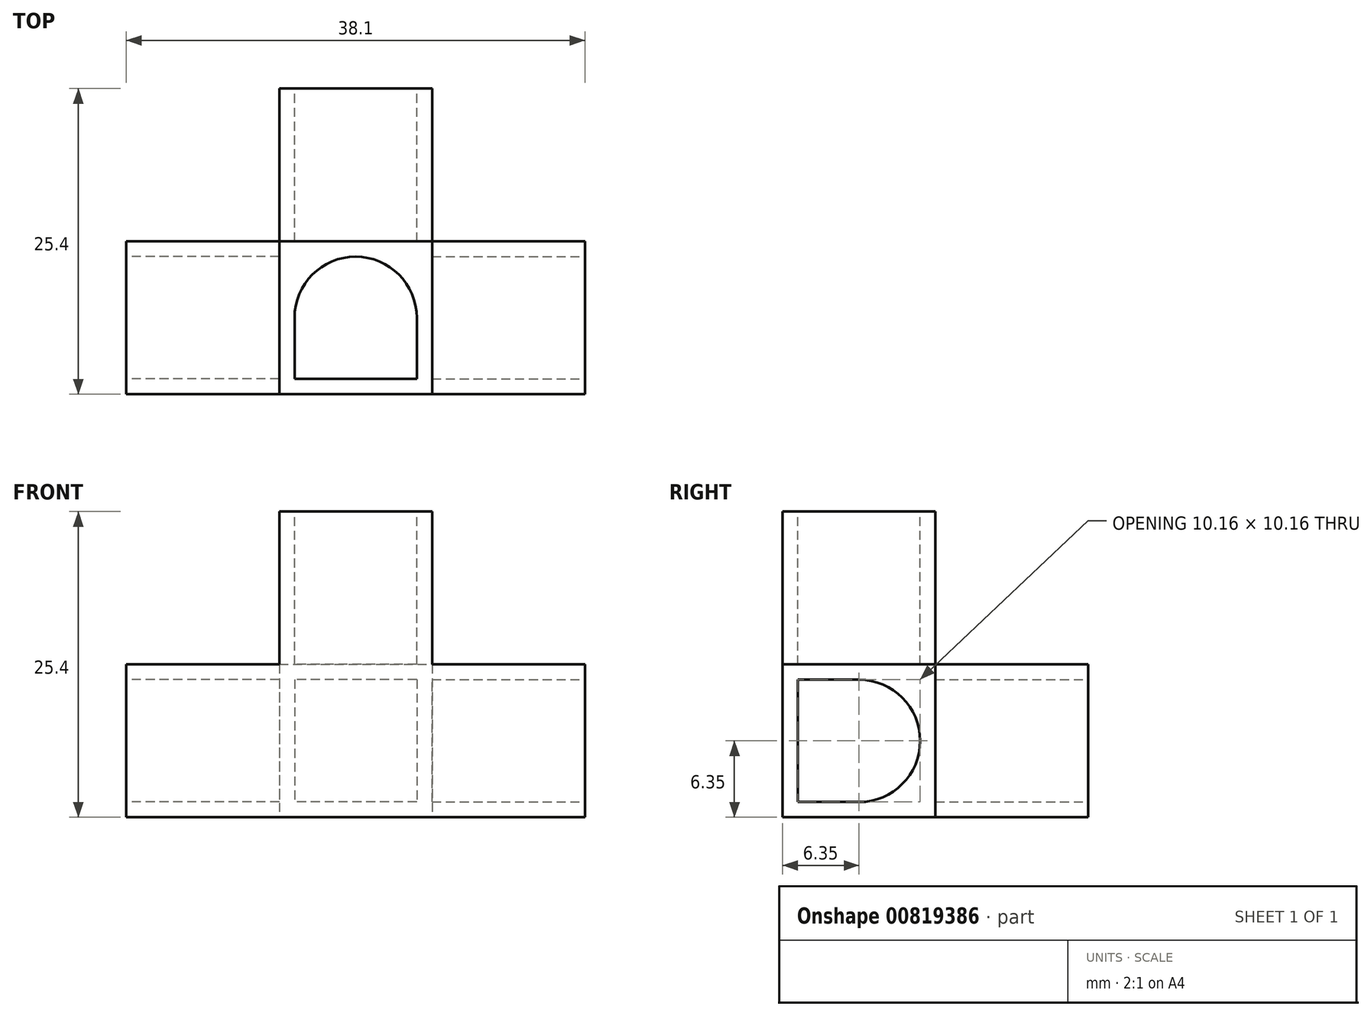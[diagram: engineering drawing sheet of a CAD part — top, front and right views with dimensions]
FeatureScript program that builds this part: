
annotation { "Feature Type Name" : "Feature", "Feature Type Description" : "" }
export const myFeature = defineFeature(function(context is Context, id is Id, definition is map)
    precondition{}
    {
        {
            var Q0;
            Q0=qCreatedBy(makeId("Top.planeOp"),FACE);
            var sketch = newSketch(context, id + "F0", { "sketchPlane" : qUnion([Q0])});
            skLineSegment(sketch, "E0", {"start": v(0, 0) * mm, "end": v(0, 12.7) * mm});
            skLineSegment(sketch, "E1", {"start": v(0, 12.7) * mm, "end": v(12.7, 12.7) * mm});
            skLineSegment(sketch, "E2", {"start": v(12.7, 12.7) * mm, "end": v(12.7, 25.4) * mm});
            skLineSegment(sketch, "E3", {"start": v(12.7, 25.4) * mm, "end": v(25.4, 25.4) * mm});
            skLineSegment(sketch, "E4", {"start": v(25.4, 25.4) * mm, "end": v(25.4, 12.7) * mm});
            skLineSegment(sketch, "E5", {"start": v(25.4, 12.7) * mm, "end": v(38.1, 12.7) * mm});
            skLineSegment(sketch, "E6", {"start": v(38.1, 12.7) * mm, "end": v(38.1, 0) * mm});
            skLineSegment(sketch, "E7", {"start": v(38.1, 0) * mm, "end": v(0, 0) * mm});
            skSolve(sketch);
        }
        {
            var Q0;
            Q0 = qSketchRegion(id + "F0", true);
            extrude(context, id + "F1", {"entities" : qUnion([Q0]), "depth" : 12.7 * mm, "offsetDistance" : 25.4 * mm});
        }
        {
            var Q0;
            Q0=makeQuery(id+"F1.opExtrude","CAP_FACE",FACE,{"disambiguationData":[OSD([sQuery(id+"F0.wireOp",EDGE,"E0"),sQuery(id+"F0.wireOp",EDGE,"E1"),sQuery(id+"F0.wireOp",EDGE,"E2"),sQuery(id+"F0.wireOp",EDGE,"E3"),sQuery(id+"F0.wireOp",EDGE,"E4"),sQuery(id+"F0.wireOp",EDGE,"E5"),sQuery(id+"F0.wireOp",EDGE,"E6"),sQuery(id+"F0.wireOp",EDGE,"E7")])],"isStart":false});
            var sketch = newSketch(context, id + "F2", { "sketchPlane" : qUnion([Q0])});
            skLineSegment(sketch, "E8.bottom", {"start": v(12.7, 12.7) * mm, "end": v(25.4, 12.7) * mm});
            skLineSegment(sketch, "E8.top", {"start": v(12.7, 0) * mm, "end": v(25.4, 0) * mm});
            skLineSegment(sketch, "E8.left", {"start": v(12.7, 12.7) * mm, "end": v(12.7, 0) * mm});
            skLineSegment(sketch, "E8.right", {"start": v(25.4, 12.7) * mm, "end": v(25.4, 0) * mm});
            skSolve(sketch);
        }
        {
            var Q0;
            Q0 = qSketchRegion(id + "F2", true);
            extrude(context, id + "F3", {"entities" : qUnion([Q0]), "operationType" : NewBodyOperationType.ADD, "depth" : 12.7 * mm, "offsetDistance" : 25.4 * mm});
        }
        {
            var Q0;
            Q0=makeQuery(id+"F1.opExtrude","SWEPT_FACE",FACE,{"disambiguationData":[OSD([sQuery(id+"F0.wireOp",EDGE,"E6")])]});
            var sketch = newSketch(context, id + "F4", { "sketchPlane" : qUnion([Q0])});
            skLineSegment(sketch, "E9.bottom", {"start": v(1.27, 1.27) * mm, "end": v(6.35, 1.27) * mm});
            skLineSegment(sketch, "E9.top", {"start": v(1.27, 11.43) * mm, "end": v(6.35, 11.43) * mm});
            skLineSegment(sketch, "E9.left", {"start": v(1.27, 1.27) * mm, "end": v(1.27, 11.43) * mm});
            skLineSegment(sketch, "E9.right", {"start": v(6.35, 1.27) * mm, "end": v(6.35, 11.43) * mm});
            skArc(sketch, "E10", {"start": v(6.35, 1.27) * mm, "mid": v(11.43, 6.35) * mm, "end": v(6.35, 11.43) * mm});
            skSolve(sketch);
        }
        {
            var Q0;
            Q0=makeQuery(id+"F1.opExtrude","SWEPT_FACE",FACE,{"disambiguationData":[OSD([sQuery(id+"F0.wireOp",EDGE,"E0")])]});
            var sketch = newSketch(context, id + "F5", { "sketchPlane" : qUnion([Q0])});
            skSolve(sketch);
        }
        {
            var Q0;
            Q0 = qSketchRegion(id + "F4", true);
            extrude(context, id + "F6", {"entities" : qUnion([Q0]), "operationType" : NewBodyOperationType.REMOVE, "oppositeDirection" : true, "depth" : 12.7 * mm, "offsetDistance" : 25.4 * mm});
        }
        {
            var Q0;
            Q0=makeQuery(id+"F3.opExtrude","CAP_FACE",FACE,{"disambiguationData":[OSD([sQuery(id+"F2.wireOp",EDGE,"E8.bottom"),sQuery(id+"F2.wireOp",EDGE,"E8.top"),sQuery(id+"F2.wireOp",EDGE,"E8.left"),sQuery(id+"F2.wireOp",EDGE,"E8.right")])],"isStart":false});
            var sketch = newSketch(context, id + "F7", { "sketchPlane" : qUnion([Q0])});
            skLineSegment(sketch, "E11.bottom", {"start": v(24.13, 1.27) * mm, "end": v(13.97, 1.27) * mm});
            skLineSegment(sketch, "E11.top", {"start": v(24.13, 6.35) * mm, "end": v(13.97, 6.35) * mm});
            skLineSegment(sketch, "E11.left", {"start": v(24.13, 1.27) * mm, "end": v(24.13, 6.35) * mm});
            skLineSegment(sketch, "E11.right", {"start": v(13.97, 1.27) * mm, "end": v(13.97, 6.35) * mm});
            skArc(sketch, "E12", {"start": v(24.13, 6.35) * mm, "mid": v(19.05, 11.43) * mm, "end": v(13.97, 6.35) * mm});
            skSolve(sketch);
        }
        {
            var Q0;
            Q0 = qSketchRegion(id + "F7", true);
            extrude(context, id + "F8", {"entities" : qUnion([Q0]), "operationType" : NewBodyOperationType.REMOVE, "oppositeDirection" : true, "depth" : 12.7 * mm, "offsetDistance" : 25.4 * mm});
        }
        {
            var Q0;
            {var subQ0=sQuery(id+"F0.wireOp",EDGE,"E0");Q0=makeQuery(id+"F5.imprint","IMPRINT",FACE,{"disambiguationData":[TD([[makeQuery(id+"F5.imprint","IMPRINT",EDGE,{"derivedFrom":makeQuery(id+"F1.opExtrude","CAP_EDGE",EDGE,{"disambiguationData":[OSD([subQ0])],"isStart":true})}),-1.0]])]});}
            var sketch = newSketch(context, id + "F9", { "sketchPlane" : qUnion([Q0])});
            skLineSegment(sketch, "E13.bottom", {"start": v(-1.27, 11.43) * mm, "end": v(-6.35, 11.43) * mm});
            skLineSegment(sketch, "E13.top", {"start": v(-1.27, 1.27) * mm, "end": v(-6.35, 1.27) * mm});
            skLineSegment(sketch, "E13.left", {"start": v(-1.27, 11.43) * mm, "end": v(-1.27, 1.27) * mm});
            skLineSegment(sketch, "E13.right", {"start": v(-6.35, 11.43) * mm, "end": v(-6.35, 1.27) * mm});
            skArc(sketch, "E14", {"start": v(-6.35, 11.43) * mm, "mid": v(-11.43, 6.35) * mm, "end": v(-6.35, 1.27) * mm});
            skSolve(sketch);
        }
        {
            var Q0;
            Q0 = qSketchRegion(id + "F9", true);
            extrude(context, id + "F10", {"entities" : qUnion([Q0]), "operationType" : NewBodyOperationType.REMOVE, "oppositeDirection" : true, "depth" : 12.7 * mm, "offsetDistance" : 25.4 * mm});
        }
        {
            var Q0;
            Q0=makeQuery(id+"F1.opExtrude","SWEPT_FACE",FACE,{"disambiguationData":[OSD([sQuery(id+"F0.wireOp",EDGE,"E3")])]});
            var sketch = newSketch(context, id + "F11", { "sketchPlane" : qUnion([Q0])});
            skLineSegment(sketch, "E15.bottom", {"start": v(-24.13, 11.43) * mm, "end": v(-13.97, 11.43) * mm});
            skLineSegment(sketch, "E15.top", {"start": v(-24.13, 1.27) * mm, "end": v(-13.97, 1.27) * mm});
            skLineSegment(sketch, "E15.left", {"start": v(-24.13, 11.43) * mm, "end": v(-24.13, 1.27) * mm});
            skLineSegment(sketch, "E15.right", {"start": v(-13.97, 11.43) * mm, "end": v(-13.97, 1.27) * mm});
            skSolve(sketch);
        }
        {
            var Q0;
            Q0 = qSketchRegion(id + "F11", true);
            extrude(context, id + "F12", {"entities" : qUnion([Q0]), "operationType" : NewBodyOperationType.REMOVE, "oppositeDirection" : true, "depth" : 12.7 * mm, "offsetDistance" : 25.4 * mm});
        }
    });
